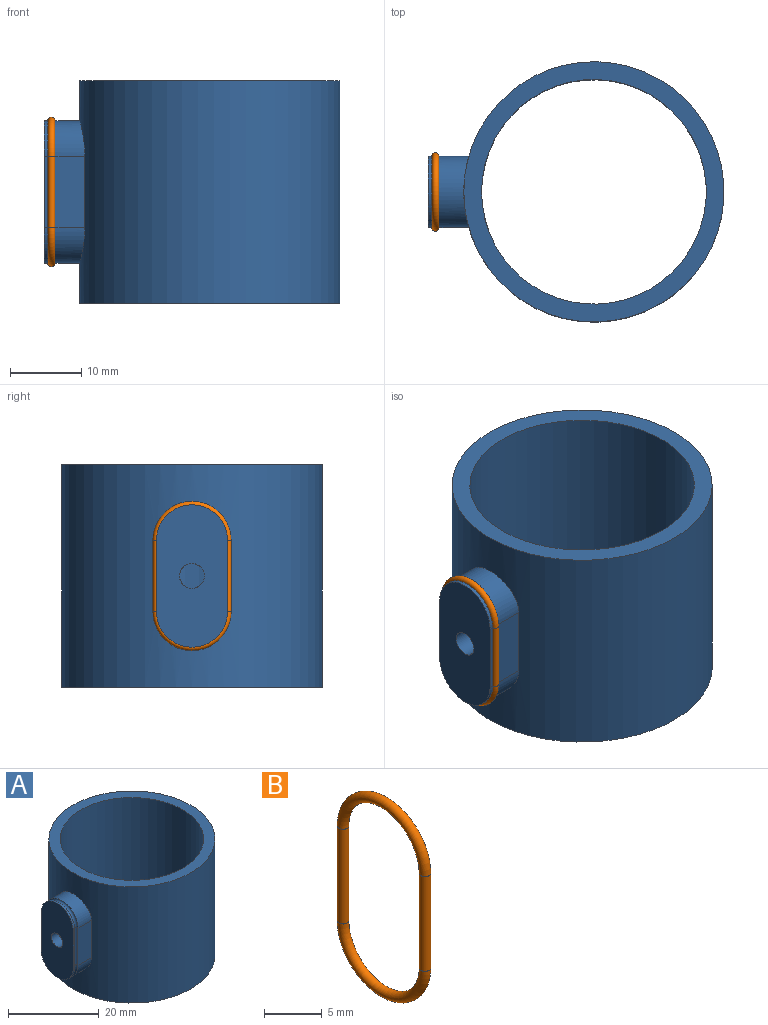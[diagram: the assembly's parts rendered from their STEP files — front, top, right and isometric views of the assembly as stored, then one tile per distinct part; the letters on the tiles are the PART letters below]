
ASSEMBLY  parts=2 mates=1
PART A: 20 faces, bbox 41.6x36.6x31.3 mm
  f0: cylinder r=5mm len=10mm, axis (-1,0,0), area 7.9mm2, adj f1,f9,f11,f17
  f1: plane 10x0.5mm, normal (0,-1,0), area 5mm2, adj f0,f3,f9,f16
  f2: plane 10x4.2mm, normal (0,1,0), area 42mm2, adj f4,f8,f12,f19
  f3: cylinder r=5mm len=10mm, axis (-1,0,0), area 7.9mm2, adj f1,f9,f11,f18
  f4: cylinder r=18.29mm len=36.58mm, axis (0,0,-1), area 3416.8mm2, adj f2,f5,f6,f8,f10,f12
  f5: cone r=18.29mm half-angle=89.7deg, axis (0,0,1), area 267.6mm2, adj f4,f7
  f6: plane 36.58x36.58mm, normal (0,0,1), area 267.6mm2, adj f4,f7
  f7: cylinder r=15.79mm len=31.58mm, axis (0,0,-1), area 3078.5mm2, adj f5,f6,f15
  f8: cylinder r=5mm len=10mm, axis (-1,0,0), area 60.4mm2, adj f2,f4,f10,f17
  f9: plane 20x10mm, normal (-1,0,0), area 168.9mm2, adj f0,f1,f3,f11,f13
  f10: plane 10x4.2mm, normal (0,-1,0), area 42mm2, adj f4,f8,f12,f16
  f11: plane 10x0.5mm, normal (0,1,0), area 5mm2, adj f0,f3,f9,f19
  f12: cylinder r=5mm len=10mm, axis (-1,0,0), area 60.4mm2, adj f2,f4,f10,f18
  f13: cylinder r=1.75mm len=5.08mm, axis (-1,0,0), area 55.4mm2, adj f9,f14
  f14: cylinder r=18.29mm len=6mm, axis (0,0,-1), area 18.7mm2, adj f13,f15
  f15: cylinder r=3mm len=6mm, axis (1,0,0), area 47.5mm2, adj f7,f14
  f16: cylinder r=0.5mm len=10mm, axis (0,0,1), area 15.7mm2, adj f1,f10,f17,f18
  f17: torus R=5mm, axis (-1,0,0), area 23.1mm2, adj f0,f8,f16,f19
  f18: torus R=5mm, axis (-1,0,0), area 23.1mm2, adj f3,f12,f16,f19
  f19: cylinder r=0.5mm len=10mm, axis (0,0,-1), area 15.7mm2, adj f2,f11,f17,f18
PART B: 4 faces, bbox 1x11.9x21.9 mm
  f0: torus R=5mm, axis (-1,0,0), area 49.3mm2, adj f1,f3
  f1: cylinder r=0.5mm len=10mm, axis (0,0,-1), area 31.4mm2, adj f0,f2
  f2: torus R=5mm, axis (-1,0,0), area 49.3mm2, adj f1,f3
  f3: cylinder r=0.5mm len=10mm, axis (0,0,1), area 31.4mm2, adj f0,f2
PLACE A t=(-22.01,-15.2,-1.58)mm
PLACE B t=(-22.01,-15.2,-1.58)mm
MATE fastened B.f3 <-> A.f16  axis (0,0,1) through (-44.3,-20.2,-1.58)mm
